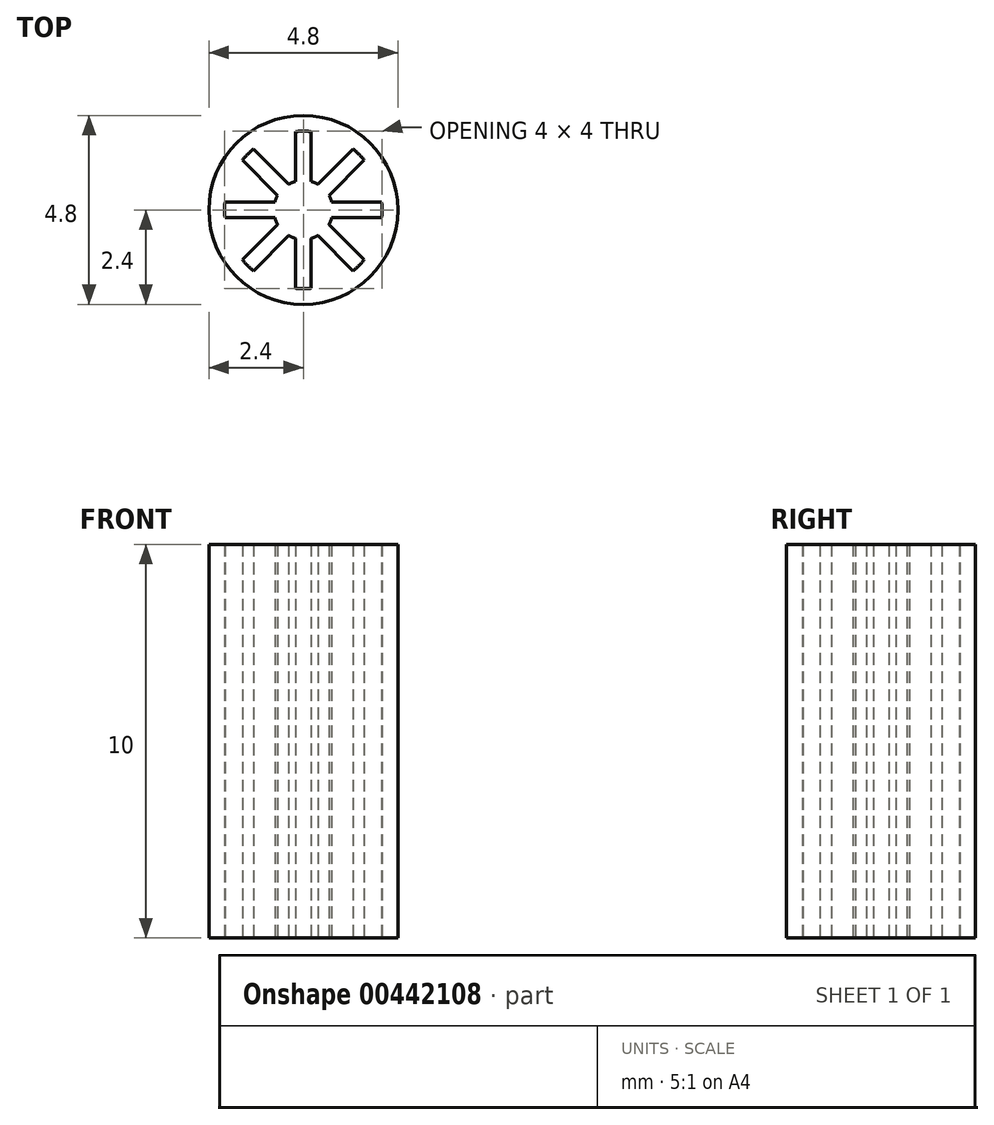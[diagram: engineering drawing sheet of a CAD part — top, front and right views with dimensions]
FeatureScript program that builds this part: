
annotation { "Feature Type Name" : "Feature", "Feature Type Description" : "" }
export const myFeature = defineFeature(function(context is Context, id is Id, definition is map)
    precondition{}
    {
        {
            var Q0;
            Q0=qCreatedBy(makeId("Top.planeOp"),FACE);
            var sketch = newSketch(context, id + "F0", { "sketchPlane" : qUnion([Q0])});
            skArc(sketch, "E0", {"start": v(-1.27, 1.55) * mm, "mid": v(-1.41, 1.41) * mm, "end": v(-1.55, 1.27) * mm});
            skArc(sketch, "E1", {"start": v(-0.65, 0.37) * mm, "mid": v(-0.7, 0.29) * mm, "end": v(-0.72, 0.2) * mm});
            skCircle(sketch, "E2", {"center": v(0, 0) * mm, "radius": 2.4 * mm});
            skLineSegment(sketch, "E3", {"start": v(0, 0) * mm, "end": v(0, 2) * mm, "construction": true});
            skLineSegment(sketch, "E4", {"start": v(-0.2, 0.72) * mm, "end": v(-0.2, 1.99) * mm});
            skLineSegment(sketch, "E5", {"start": v(0, 0) * mm, "end": v(-1.41, 1.41) * mm, "construction": true});
            skLineSegment(sketch, "E6", {"start": v(0, 0) * mm, "end": v(-2, 0) * mm, "construction": true});
            skLineSegment(sketch, "E7", {"start": v(-1.27, 1.55) * mm, "end": v(-0.37, 0.65) * mm});
            skLineSegment(sketch, "E8.MirrorCS", {"start": v(-1.55, 1.27) * mm, "end": v(-0.65, 0.37) * mm});
            skLineSegment(sketch, "E9.MirrorCS", {"start": v(-0.72, 0.2) * mm, "end": v(-1.99, 0.2) * mm});
            skLineSegment(sketch, "E10.MirrorCS", {"start": v(-0.72, -0.2) * mm, "end": v(-1.99, -0.2) * mm});
            skLineSegment(sketch, "E11.MirrorCS", {"start": v(-1.55, -1.27) * mm, "end": v(-0.65, -0.37) * mm});
            skLineSegment(sketch, "E12.MirrorCS", {"start": v(-0.2, -0.72) * mm, "end": v(-0.2, -1.99) * mm});
            skLineSegment(sketch, "E13.MirrorCS", {"start": v(-1.27, -1.55) * mm, "end": v(-0.37, -0.65) * mm});
            skLineSegment(sketch, "E14.MirrorCS", {"start": v(0.2, 0.72) * mm, "end": v(0.2, 1.99) * mm});
            skLineSegment(sketch, "E15.MirrorCS", {"start": v(1.27, 1.55) * mm, "end": v(0.37, 0.65) * mm});
            skLineSegment(sketch, "E16.MirrorCS", {"start": v(1.55, 1.27) * mm, "end": v(0.65, 0.37) * mm});
            skLineSegment(sketch, "E17.MirrorCS", {"start": v(0.72, 0.2) * mm, "end": v(1.99, 0.2) * mm});
            skLineSegment(sketch, "E18.MirrorCS", {"start": v(0.72, -0.2) * mm, "end": v(1.99, -0.2) * mm});
            skLineSegment(sketch, "E19.MirrorCS", {"start": v(1.55, -1.27) * mm, "end": v(0.65, -0.37) * mm});
            skLineSegment(sketch, "E20.MirrorCS", {"start": v(1.27, -1.55) * mm, "end": v(0.37, -0.65) * mm});
            skLineSegment(sketch, "E21.MirrorCS", {"start": v(0.2, -0.72) * mm, "end": v(0.2, -1.99) * mm});
            skArc(sketch, "E22.trimOffspring", {"start": v(0.2, 1.99) * mm, "mid": v(0, 2) * mm, "end": v(-0.2, 1.99) * mm});
            skArc(sketch, "E23.trimOffspring", {"start": v(1.55, 1.27) * mm, "mid": v(1.41, 1.41) * mm, "end": v(1.27, 1.55) * mm});
            skArc(sketch, "E24.trimOffspring", {"start": v(1.99, -0.2) * mm, "mid": v(2, 0) * mm, "end": v(1.99, 0.2) * mm});
            skArc(sketch, "E25.trimOffspring", {"start": v(1.27, -1.55) * mm, "mid": v(1.41, -1.41) * mm, "end": v(1.55, -1.27) * mm});
            skArc(sketch, "E26.trimOffspring", {"start": v(-0.2, -1.99) * mm, "mid": v(0, -2) * mm, "end": v(0.2, -1.99) * mm});
            skArc(sketch, "E27.trimOffspring", {"start": v(-1.55, -1.27) * mm, "mid": v(-1.41, -1.41) * mm, "end": v(-1.27, -1.55) * mm});
            skArc(sketch, "E28.trimOffspring", {"start": v(-1.99, 0.2) * mm, "mid": v(-2, 0) * mm, "end": v(-1.99, -0.2) * mm});
            skArc(sketch, "E29.trimOffspring", {"start": v(-0.2, 0.72) * mm, "mid": v(-0.29, 0.7) * mm, "end": v(-0.37, 0.65) * mm});
            skArc(sketch, "E30.trimOffspring", {"start": v(0.37, 0.65) * mm, "mid": v(0.29, 0.7) * mm, "end": v(0.2, 0.72) * mm});
            skArc(sketch, "E31.trimOffspring", {"start": v(0.72, 0.2) * mm, "mid": v(0.7, 0.29) * mm, "end": v(0.65, 0.37) * mm});
            skArc(sketch, "E32.trimOffspring", {"start": v(0.65, -0.37) * mm, "mid": v(0.7, -0.29) * mm, "end": v(0.72, -0.2) * mm});
            skArc(sketch, "E33.trimOffspring", {"start": v(0.2, -0.72) * mm, "mid": v(0.29, -0.7) * mm, "end": v(0.37, -0.65) * mm});
            skArc(sketch, "E34.trimOffspring", {"start": v(-0.37, -0.65) * mm, "mid": v(-0.29, -0.7) * mm, "end": v(-0.2, -0.72) * mm});
            skArc(sketch, "E35.trimOffspring", {"start": v(-0.72, -0.2) * mm, "mid": v(-0.7, -0.29) * mm, "end": v(-0.65, -0.37) * mm});
            skSolve(sketch);
        }
        {
            var Q0;
            Q0=makeQuery(id+"F0.imprint","IMPRINT",FACE,{"disambiguationData":[TD([[makeQuery(id+"F0.imprint","IMPRINT",EDGE,{"derivedFrom":sQuery(id+"F0.wireOp",EDGE,"E0")}),-1.0]])]});
            extrude(context, id + "F1", {"entities" : qUnion([Q0]), "depth" : 10 * mm});
        }
    });
